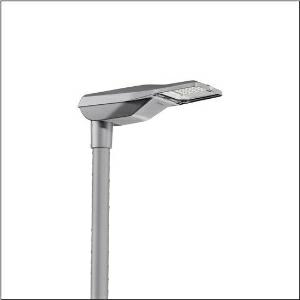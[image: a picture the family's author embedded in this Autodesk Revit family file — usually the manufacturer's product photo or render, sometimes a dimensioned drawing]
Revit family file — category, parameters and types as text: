
# Revit family: streetlight_sl_21_iq_micro___p0_8ab_5xe1r31g08db_e4e9
name_source: partatom
category: Lighting Fixtures
units: mm (PartAtom-declared; Revit-internal decimal feet)

## family parameters
Cut with Voids When Loaded = No
Host = Face
Light Source = No
Part Type = Normal
Room Calculation Point = No
Round Connector Dimension = Use Diameter
Shared = No

## types (1)
- --- (1 x LED, 4220 lm, 36.4 W, 3000K)
    Apparent Load = 36 VA
    CIE Flux Codes = 36 71 98 100 100
    Color Rendering = 70
    Color Temperature = 3000K
    Default Elevation = 1800 mm
    Description = Streetlight SL 21 iQ micro, mast luminaire, primary light control with lens, of PMMA, primary optical cover: cover, of toughened safety glass, transparent, light distribution: P0.8aB, light emission: direct distribution, primary light characteristic: asymmetric, installation type: post-top, side-entry, LED, High Power LED, rated luminous flux: 4.220lm, luminous efficacy: 116lm/W, light colour: 730, colour temperature: 3000K, control gear: iQ Street-Remote, control: pre-setting: linear dimming characteristic, Street-Remote, Auto-Match, Temp-Guard, Lumen-Switch, Night-Set, Smart-Wire, Light-Fading, Desk-Remote (wireless, voltage-free reading and setting of iQ features in the workshop via application-optimized NFC function/RFID function), optimised constant luminous flux control (CLO 2.0), mains connection: 220..240V, AC, 50/60Hz, start of lifetime: 36W, end of service life: 38W, reduction: 16W, luminaire housing, of diecast aluminium, powder-coated, Siteco® metallic grey (DB 702S), corrosivity category C5 mid according to DIN EN ISO 12944, please order mast flange separately, inclination adjustable: 0°, 5°, 10°, 15°, sealing non-destructively replaceable, multi-level sealing system, length: 528mm, width: 235mm, height: 110mm, mast flange for spigot size: 42mm (side-entry): 5XC10008XM4, 60/48mm (side-entry/post-top): 5XC10108XM2, 76/60mm (side-entry/post-top): 5XC10108XM1, protection rating (complete): IP66, insulation class (complete): insulation class II (safety insulation), certification: CE, ENEC, ENEC+, VDE, impact resistance: IK10, permissible operating ambient temperature for outdoor applications: -40..+50°C, standard-compliant lighting for roads and squares, packaging unit: 1 piece

Light Distribution: P0.8aB
    Height = 110 mm
    Lamp = 1 x LED
    Lamp Light Flux = 4220 lm
    Lamp Power = 36.4 W
    Lamp count = 1
    Length = 528 mm
    Luminous efficacy = 116 lm/W
    Manufacturer = Siteco
    ModVariant = No
    Model = 5XE1R31G08DB
    Number of Poles = 1
    OnlyDefault = Yes
    Power Factor = 1
    Product Name = Streetlight SL 21 iQ micro | P0.8aB
    Product group = mast luminaire | pylon top
    ProductGroupID = 6100
    Protection Class = Protection class II
    Protection Degree = IP 66
    RLX_Detail_Level = 1
    RLX_Emergency_Light_Flux = 0 lm
    RLX_Emergency_Type = 0
    RLX_Emergency_Type_DB = No
    RlxData = <blob elided: 99189 chars, md5=d6f5c2c0>
    Socket = socket
    Standby Power = 0 W
    System Light Flux = 4220 lm
    System Power = 36 W
    Type Comments = factory setting: luminous flux: 100 % | dim-lin: 254 | 715 mA
    Type Image = l_1006881.jpg
    URL = http://relux.com
    VarID = @adj_096307
    Voltage = 0 V
    Weight = 0.00 kg
    Width = 235 mm

## geometry (parser evidence)
native form markers: Blend x4, Sweep x11
no freeform markers — native parametric forms only
